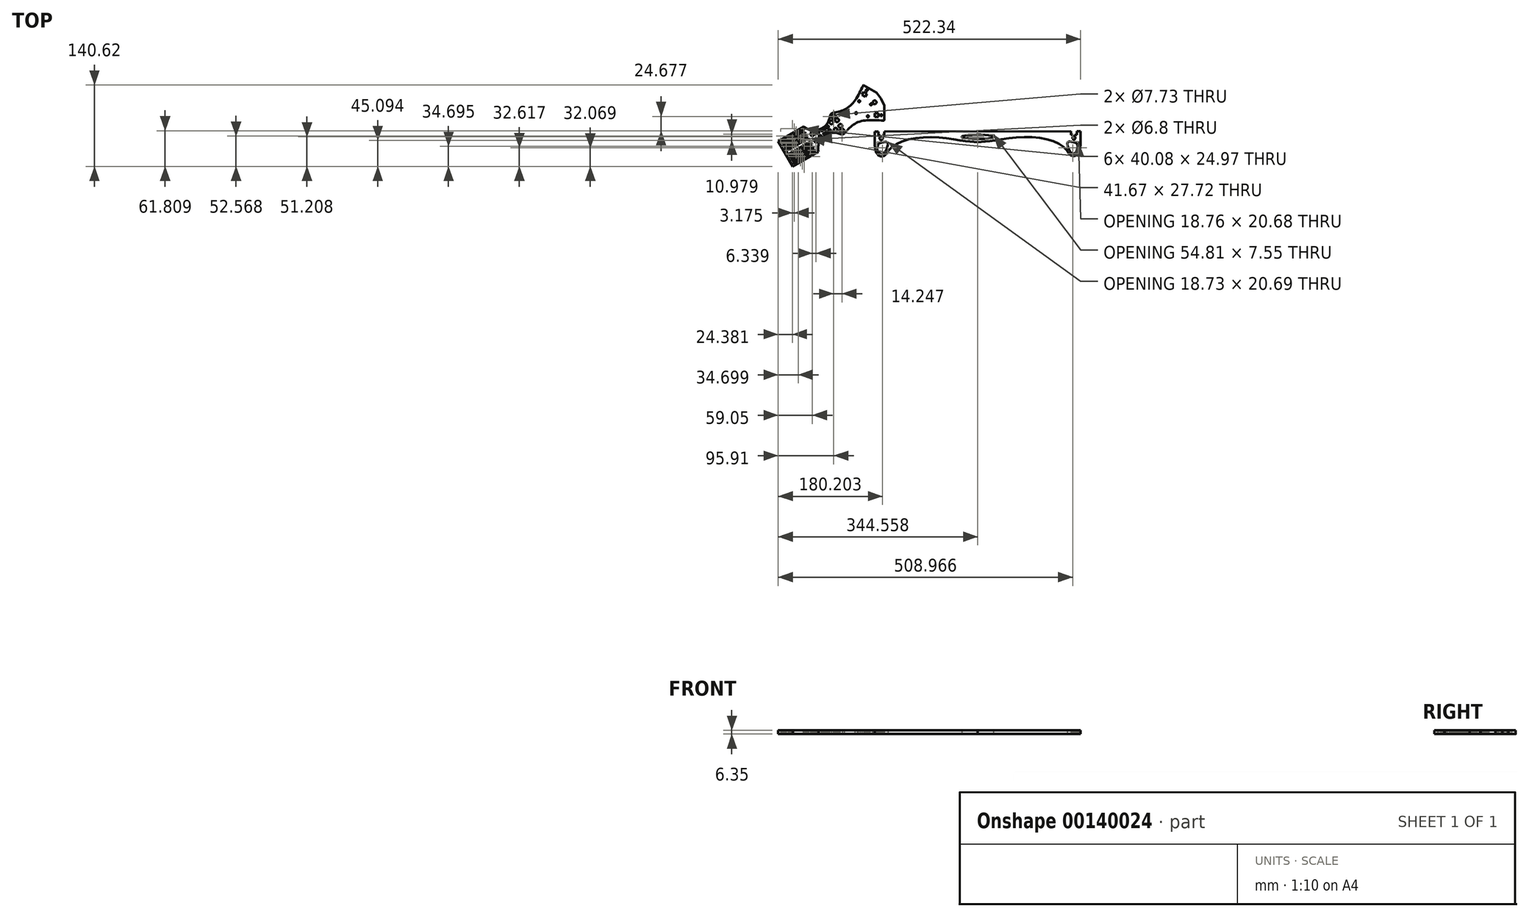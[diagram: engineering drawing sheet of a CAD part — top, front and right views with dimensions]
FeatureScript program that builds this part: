
annotation { "Feature Type Name" : "Feature", "Feature Type Description" : "" }
export const myFeature = defineFeature(function(context is Context, id is Id, definition is map)
    precondition{}
    {
        {
            var Q0;
            Q0=qCreatedBy(makeId("Top.planeOp"),FACE);
            var sketch = newSketch(context, id + "F0", { "sketchPlane" : qUnion([Q0])});
            skLineSegment(sketch, "E0.0", {"start": v(-166.81, -70.9) * mm, "end": v(-163.64, -65.4) * mm, "construction": true});
            skArc(sketch, "E1", {"start": v(-198.63, -138.44) * mm, "mid": v(-199.81, -115.36) * mm, "end": v(-219.2, -102.8) * mm, "construction": true});
            skLineSegment(sketch, "E2", {"start": v(-311.5, -150.52) * mm, "end": v(-298.8, -172.51) * mm});
            skLineSegment(sketch, "E3.MirrorCS", {"start": v(-286.1, -194.51) * mm, "end": v(-298.8, -172.51) * mm});
            skLineSegment(sketch, "E4", {"start": v(-311.5, -150.52) * mm, "end": v(-267.5, -125.12) * mm});
            skLineSegment(sketch, "E5", {"start": v(-242.1, -169.11) * mm, "end": v(-286.1, -194.51) * mm});
            skCircle(sketch, "E6", {"center": v(-144.81, -83.61) * mm, "radius": 3.18 * mm});
            skLineSegment(sketch, "E7", {"start": v(-144.81, -83.61) * mm, "end": v(-133.8, -77.26) * mm, "construction": true});
            skArc(sketch, "E8", {"start": v(-267.5, -125.12) * mm, "mid": v(-239.3, -130.06) * mm, "end": v(-221.9, -107.34) * mm});
            skArc(sketch, "E9.MirrorCS", {"start": v(-242.1, -169.11) * mm, "mid": v(-232.29, -142.22) * mm, "end": v(-203.9, -138.51) * mm});
            skLineSegment(sketch, "E10", {"start": v(-161.31, -74.07) * mm, "end": v(-166.81, -70.9) * mm});
            skLineSegment(sketch, "E11", {"start": v(-161.31, -74.07) * mm, "end": v(-144.81, -83.61) * mm, "construction": true});
            skLineSegment(sketch, "E12", {"start": v(-166.81, -70.9) * mm, "end": v(-163.64, -65.4) * mm});
            skFitSpline(sketch, "E13", {"points": [v(-199.81, -140.75) * mm, v(-173.7, -118.02) * mm, v(-128.63, -115.42) * mm], "startDerivative": vector(49.2, 58.94) * mm, "endDerivative": vector(92.18, -6.8) * mm});
            skFitSpline(sketch, "E14.MirrorCS", {"points": [v(-221.8, -102.67) * mm, v(-189.06, -91.43) * mm, v(-164.26, -53.69) * mm], "startDerivative": vector(75.64, 13.15) * mm, "endDerivative": vector(40.2, 83.23) * mm});
            skFitSpline(sketch, "E15.MirrorCS", {"points": [v(-221.8, -102.67) * mm, v(-189.06, -91.43) * mm, v(-164.26, -53.69) * mm], "startDerivative": vector(75.64, 13.15) * mm, "endDerivative": vector(40.2, 83.23) * mm});
            skArc(sketch, "E16.filletArc", {"start": v(-203.9, -138.51) * mm, "mid": v(-199.93, -138.9) * mm, "end": v(-196.5, -136.82) * mm});
            skArc(sketch, "E17.filletArc", {"start": v(-216.74, -101.78) * mm, "mid": v(-220.24, -103.7) * mm, "end": v(-221.9, -107.34) * mm});
            skArc(sketch, "E18.filletArc", {"start": v(-163.42, -53.93) * mm, "mid": v(-164.13, -53.98) * mm, "end": v(-164.64, -54.47) * mm});
            skArc(sketch, "E19.filletArc", {"start": v(-129.49, -115.35) * mm, "mid": v(-128.8, -115.16) * mm, "end": v(-128.41, -114.57) * mm});
            skLineSegment(sketch, "E20.MirrorCS", {"start": v(-144.8, -102.67) * mm, "end": v(-144.8, -109.02) * mm});
            skLineSegment(sketch, "E21", {"start": v(-144.8, -102.67) * mm, "end": v(-138.45, -102.67) * mm});
            skLineSegment(sketch, "E22.0", {"start": v(-283.35, -192.92) * mm, "end": v(-296.05, -170.93) * mm, "construction": true});
            skLineSegment(sketch, "E23.0", {"start": v(-259.14, -145.95) * mm, "end": v(-297.64, -168.18) * mm});
            skLineSegment(sketch, "E24.0", {"start": v(-260.73, -143.2) * mm, "end": v(-299.22, -165.43) * mm});
            skLineSegment(sketch, "E25.0", {"start": v(-262.32, -140.45) * mm, "end": v(-300.81, -162.68) * mm});
            skLineSegment(sketch, "E26.0", {"start": v(-263.9, -137.7) * mm, "end": v(-302.4, -159.93) * mm});
            skLineSegment(sketch, "E27.0", {"start": v(-265.5, -134.95) * mm, "end": v(-303.99, -157.18) * mm});
            skLineSegment(sketch, "E28.0", {"start": v(-267.08, -132.2) * mm, "end": v(-305.57, -154.43) * mm});
            skLineSegment(sketch, "E29.0", {"start": v(-268.67, -129.45) * mm, "end": v(-307.16, -151.68) * mm});
            skLineSegment(sketch, "E30.0", {"start": v(-268.67, -129.45) * mm, "end": v(-267.08, -132.2) * mm});
            skLineSegment(sketch, "E31.trimOffspring", {"start": v(-259.14, -145.95) * mm, "end": v(-257.55, -148.7) * mm});
            skLineSegment(sketch, "E32.trimOffspring", {"start": v(-262.32, -140.45) * mm, "end": v(-260.73, -143.2) * mm});
            skLineSegment(sketch, "E33.trimOffspring", {"start": v(-265.5, -134.95) * mm, "end": v(-263.9, -137.7) * mm});
            skLineSegment(sketch, "E34", {"start": v(-296.05, -170.93) * mm, "end": v(-297.64, -168.18) * mm});
            skLineSegment(sketch, "E35", {"start": v(-299.22, -165.43) * mm, "end": v(-300.81, -162.68) * mm});
            skLineSegment(sketch, "E36", {"start": v(-302.4, -159.93) * mm, "end": v(-303.99, -157.18) * mm});
            skLineSegment(sketch, "E37", {"start": v(-305.57, -154.43) * mm, "end": v(-307.16, -151.68) * mm});
            skLineSegment(sketch, "E38.MirrorCS", {"start": v(-254.38, -154.2) * mm, "end": v(-292.87, -176.43) * mm});
            skLineSegment(sketch, "E39.MirrorCS", {"start": v(-252.8, -156.95) * mm, "end": v(-291.29, -179.18) * mm});
            skLineSegment(sketch, "E40.MirrorCS", {"start": v(-252.8, -156.95) * mm, "end": v(-254.38, -154.2) * mm});
            skLineSegment(sketch, "E41.MirrorCS", {"start": v(-292.87, -176.43) * mm, "end": v(-291.29, -179.18) * mm});
            skLineSegment(sketch, "E42.MirrorCS", {"start": v(-289.7, -181.93) * mm, "end": v(-288.11, -184.68) * mm});
            skLineSegment(sketch, "E43.MirrorCS", {"start": v(-251.2, -159.7) * mm, "end": v(-289.7, -181.93) * mm});
            skLineSegment(sketch, "E44.MirrorCS", {"start": v(-249.62, -162.45) * mm, "end": v(-288.11, -184.68) * mm});
            skLineSegment(sketch, "E45.MirrorCS", {"start": v(-249.62, -162.45) * mm, "end": v(-251.2, -159.7) * mm});
            skLineSegment(sketch, "E46.MirrorCS", {"start": v(-246.44, -167.95) * mm, "end": v(-248.03, -165.2) * mm});
            skLineSegment(sketch, "E47.MirrorCS", {"start": v(-248.03, -165.2) * mm, "end": v(-286.52, -187.43) * mm});
            skLineSegment(sketch, "E48.MirrorCS", {"start": v(-246.44, -167.95) * mm, "end": v(-284.94, -190.17) * mm});
            skLineSegment(sketch, "E49.MirrorCS", {"start": v(-286.52, -187.43) * mm, "end": v(-284.94, -190.17) * mm});
            skLineSegment(sketch, "E50.MirrorCS", {"start": v(-255.97, -151.45) * mm, "end": v(-294.46, -173.68) * mm});
            skLineSegment(sketch, "E51.MirrorCS", {"start": v(-255.97, -151.45) * mm, "end": v(-257.55, -148.7) * mm});
            skLineSegment(sketch, "E52.MirrorCS", {"start": v(-296.05, -170.93) * mm, "end": v(-294.46, -173.68) * mm});
            skCircle(sketch, "E53", {"center": v(-252.45, -138.44) * mm, "radius": 3.4 * mm});
            skCircle(sketch, "E54", {"center": v(-243.01, -135.53) * mm, "radius": 2.34 * mm});
            skCircle(sketch, "E55", {"center": v(-235.75, -132.08) * mm, "radius": 1.52 * mm});
            skCircle(sketch, "E56", {"center": v(-230.85, -130.06) * mm, "radius": 1.01 * mm});
            skCircle(sketch, "E57", {"center": v(-226.2, -126.02) * mm, "radius": 2.4 * mm});
            skCircle(sketch, "E58", {"center": v(-219.6, -118.34) * mm, "radius": 3.08 * mm});
            skCircle(sketch, "E59", {"center": v(-215.6, -108.02) * mm, "radius": 3.86 * mm});
            skCircle(sketch, "E60.MirrorC", {"center": v(-246.11, -149.42) * mm, "radius": 3.4 * mm});
            skCircle(sketch, "E61.MirrorC", {"center": v(-238.88, -142.7) * mm, "radius": 2.34 * mm});
            skCircle(sketch, "E62.MirrorC", {"center": v(-232.26, -138.13) * mm, "radius": 1.52 * mm});
            skCircle(sketch, "E63.MirrorC", {"center": v(-228.06, -134.9) * mm, "radius": 1.01 * mm});
            skCircle(sketch, "E64.MirrorC", {"center": v(-222.23, -132.88) * mm, "radius": 2.4 * mm});
            skCircle(sketch, "E65.MirrorC", {"center": v(-212.28, -131.01) * mm, "radius": 3.08 * mm});
            skCircle(sketch, "E66.MirrorC", {"center": v(-201.34, -132.7) * mm, "radius": 3.86 * mm});
            skCircle(sketch, "E67", {"center": v(-209.78, -114.53) * mm, "radius": 3.25 * mm});
            skCircle(sketch, "E68.MirrorC", {"center": v(-204.08, -124.42) * mm, "radius": 3.25 * mm});
            skLineSegment(sketch, "E69.MirrorCS", {"start": v(-138.45, -102.67) * mm, "end": v(-138.45, -109) * mm});
            skLineSegment(sketch, "E70", {"start": v(-163.42, -53.93) * mm, "end": v(-141.42, -66.62) * mm});
            skLineSegment(sketch, "E71", {"start": v(-141.42, -66.62) * mm, "end": v(-133.8, -77.26) * mm});
            skLineSegment(sketch, "E72.MirrorCS", {"start": v(-128.4, -89.17) * mm, "end": v(-133.8, -77.26) * mm});
            skLineSegment(sketch, "E73.MirrorCS", {"start": v(-128.41, -114.57) * mm, "end": v(-128.4, -89.17) * mm});
            skLineSegment(sketch, "E74", {"start": v(-144.8, -109.02) * mm, "end": v(-138.45, -109) * mm});
            skLineSegment(sketch, "E75.trimOffspring", {"start": v(-163.64, -65.4) * mm, "end": v(-166.81, -70.9) * mm});
            skLineSegment(sketch, "E76", {"start": v(-161.31, -74.07) * mm, "end": v(-158.14, -68.57) * mm});
            skLineSegment(sketch, "E77.0", {"start": v(-144.76, -134.08) * mm, "end": v(-138.45, -134.07) * mm});
            skLineSegment(sketch, "E78", {"start": v(-144.76, -134.08) * mm, "end": v(-144.7, -146.63) * mm});
            skLineSegment(sketch, "E79", {"start": v(-138.45, -140.42) * mm, "end": v(-138.45, -134.07) * mm});
            skLineSegment(sketch, "E80.trimOffspring", {"start": v(-128.33, -134.05) * mm, "end": v(33.04, -133.78) * mm});
            skLineSegment(sketch, "E81", {"start": v(-128.32, -140.4) * mm, "end": v(-128.33, -134.05) * mm});
            skLineSegment(sketch, "E82", {"start": v(33.07, -152.83) * mm, "end": v(33.04, -133.78) * mm, "construction": true});
            skPoint(sketch, "E83.orphan", {"position": v(33.06, -143.3) * mm});
            skLineSegment(sketch, "E84", {"start": v(-138.45, -105.84) * mm, "end": v(-128.4, -105.84) * mm, "construction": true});
            skCircle(sketch, "E85", {"center": v(-133.43, -105.84) * mm, "radius": 1.46 * mm});
            skLineSegment(sketch, "E86.MirrorCS", {"start": v(-134.89, -140.41) * mm, "end": v(-134.9, -144.56) * mm});
            skLineSegment(sketch, "E87.MirrorCS", {"start": v(-134.9, -144.56) * mm, "end": v(-136.17, -144.56) * mm});
            skLineSegment(sketch, "E88.MirrorCS", {"start": v(-136.17, -144.56) * mm, "end": v(-136.18, -147.1) * mm});
            skLineSegment(sketch, "E89.MirrorCS", {"start": v(-136.18, -147.1) * mm, "end": v(-134.9, -147.1) * mm});
            skLineSegment(sketch, "E90.MirrorCS", {"start": v(-134.9, -147.1) * mm, "end": v(-134.91, -149.33) * mm});
            skLineSegment(sketch, "E91.MirrorCS", {"start": v(-132, -149.33) * mm, "end": v(-134.91, -149.33) * mm});
            skLineSegment(sketch, "E92.MirrorCS", {"start": v(-132, -149.33) * mm, "end": v(-131.99, -147.11) * mm});
            skLineSegment(sketch, "E93.MirrorCS", {"start": v(-131.99, -147.11) * mm, "end": v(-130.72, -147.12) * mm});
            skLineSegment(sketch, "E94.MirrorCS", {"start": v(-130.72, -147.12) * mm, "end": v(-130.71, -144.58) * mm});
            skLineSegment(sketch, "E95.MirrorCS", {"start": v(-130.71, -144.58) * mm, "end": v(-131.98, -144.57) * mm});
            skLineSegment(sketch, "E96.MirrorCS", {"start": v(-131.98, -144.57) * mm, "end": v(-131.97, -140.42) * mm});
            skLineSegment(sketch, "E97", {"start": v(-138.45, -140.42) * mm, "end": v(-134.89, -140.41) * mm});
            skLineSegment(sketch, "E98", {"start": v(-131.97, -140.42) * mm, "end": v(-128.32, -140.4) * mm});
            skCircle(sketch, "E99.MirrorC", {"center": v(-158.37, -62.64) * mm, "radius": 1.46 * mm});
            skFitSpline(sketch, "E100", {"points": [v(-144.7, -146.63) * mm, v(-140.33, -173.45) * mm, v(-129.21, -176.66) * mm, v(-115.84, -161.59) * mm, v(-60.45, -144.07) * mm, v(9.62, -150.28) * mm, v(33.07, -152.83) * mm], "startDerivative": vector(-0.17, -209.32) * mm, "endDerivative": vector(140.7, -11.73) * mm});
            skLineSegment(sketch, "E101.MirrorCS", {"start": v(194.41, -133.5) * mm, "end": v(33.04, -133.78) * mm});
            skLineSegment(sketch, "E102.MirrorCS", {"start": v(194.42, -139.86) * mm, "end": v(194.41, -133.5) * mm});
            skLineSegment(sketch, "E103.MirrorCS", {"start": v(198.07, -139.86) * mm, "end": v(194.42, -139.86) * mm});
            skLineSegment(sketch, "E104.MirrorCS", {"start": v(198.1, -144.02) * mm, "end": v(198.07, -139.86) * mm});
            skLineSegment(sketch, "E105.MirrorCS", {"start": v(196.83, -144.02) * mm, "end": v(198.1, -144.02) * mm});
            skLineSegment(sketch, "E106.MirrorCS", {"start": v(196.85, -146.56) * mm, "end": v(196.83, -144.02) * mm});
            skLineSegment(sketch, "E107.MirrorCS", {"start": v(198.12, -146.56) * mm, "end": v(196.85, -146.56) * mm});
            skLineSegment(sketch, "E108.MirrorCS", {"start": v(198.13, -148.78) * mm, "end": v(198.12, -146.56) * mm});
            skLineSegment(sketch, "E109.MirrorCS", {"start": v(198.13, -148.78) * mm, "end": v(201.05, -148.76) * mm});
            skLineSegment(sketch, "E110.MirrorCS", {"start": v(201.04, -146.54) * mm, "end": v(201.05, -148.76) * mm});
            skLineSegment(sketch, "E111.MirrorCS", {"start": v(202.3, -146.53) * mm, "end": v(201.04, -146.54) * mm});
            skLineSegment(sketch, "E112.MirrorCS", {"start": v(202.3, -144) * mm, "end": v(202.3, -146.53) * mm});
            skLineSegment(sketch, "E113.MirrorCS", {"start": v(201.02, -144) * mm, "end": v(202.3, -144) * mm});
            skLineSegment(sketch, "E114.MirrorCS", {"start": v(201, -139.85) * mm, "end": v(201.02, -144) * mm});
            skLineSegment(sketch, "E115.MirrorCS", {"start": v(204.56, -139.84) * mm, "end": v(201, -139.85) * mm});
            skLineSegment(sketch, "E116.MirrorCS", {"start": v(204.56, -139.84) * mm, "end": v(204.53, -133.49) * mm});
            skLineSegment(sketch, "E117.MirrorCS", {"start": v(210.84, -133.48) * mm, "end": v(210.83, -146.03) * mm});
            skFitSpline(sketch, "E118.MirrorCS", {"points": [v(210.83, -146.03) * mm, v(206.54, -172.87) * mm, v(195.44, -176.11) * mm, v(182.02, -161.09) * mm, v(126.57, -143.75) * mm, v(56.52, -150.2) * mm, v(33.07, -152.83) * mm], "startDerivative": vector(0.87, -209.32) * mm, "endDerivative": vector(-140.66, -12.2) * mm});
            skLineSegment(sketch, "E119", {"start": v(204.53, -133.49) * mm, "end": v(210.84, -133.48) * mm});
            skLineSegment(sketch, "E120", {"start": v(-144.81, -83.61) * mm, "end": v(-147.56, -85.2) * mm, "construction": true});
            skCircle(sketch, "E121", {"center": v(-164.01, -94.7) * mm, "radius": 19 * mm, "construction": true});
            skCircle(sketch, "E122", {"center": v(-177.01, -102.2) * mm, "radius": 1.65 * mm});
            skCircle(sketch, "E123", {"center": v(-156.5, -107.7) * mm, "radius": 1.65 * mm});
            skCircle(sketch, "E124.MirrorC", {"center": v(-171.52, -81.7) * mm, "radius": 1.65 * mm});
            skCircle(sketch, "E125.MirrorC", {"center": v(-151.01, -87.2) * mm, "radius": 1.65 * mm});
            skFitSpline(sketch, "E126", {"points": [v(-139, -157.22) * mm, v(-137.34, -154.8) * mm, v(-127.5, -152.1) * mm, v(-122, -154.28) * mm, v(-129.54, -172.05) * mm, v(-137.2, -170.26) * mm, v(-140.66, -163.36) * mm, v(-139, -157.22) * mm]});
            skEllipse(sketch, "E127", {"center": v(33.06, -143.3) * mm, "majorRadius": 3.77 * mm, "minorRadius": 27.4 * mm, "majorAxis": v(0, -1)});
            skFitSpline(sketch, "E128.MirrorC", {"points": [v(205.16, -156.64) * mm, v(203.5, -154.22) * mm, v(193.64, -151.57) * mm, v(188.15, -153.76) * mm, v(195.75, -171.5) * mm, v(203.42, -169.69) * mm, v(206.84, -162.77) * mm, v(205.16, -156.64) * mm]});
            skLineSegment(sketch, "E129", {"start": v(-163.64, -65.4) * mm, "end": v(-158.14, -68.57) * mm});
            skSolve(sketch);
        }
        {
            var Q0;
            Q0=makeQuery(id+"F0.imprint","IMPRINT",FACE,{"disambiguationData":[TD([[makeQuery(id+"F0.imprint","IMPRINT",EDGE,{"derivedFrom":sQuery(id+"F0.wireOp",EDGE,"E77.0")}),-1.0]])]});
            extrude(context, id + "F1", {"entities" : qUnion([Q0]), "depth" : 6.35 * mm});
        }
        {
            var Q0;
            Q0=makeQuery(id+"F0.imprint","IMPRINT",FACE,{"disambiguationData":[TD([[makeQuery(id+"F0.imprint","IMPRINT",EDGE,{"derivedFrom":sQuery(id+"F0.wireOp",EDGE,"E2")}),1.0]])]});
            extrude(context, id + "F2", {"entities" : qUnion([Q0]), "depth" : 6.35 * mm});
        }
    });
